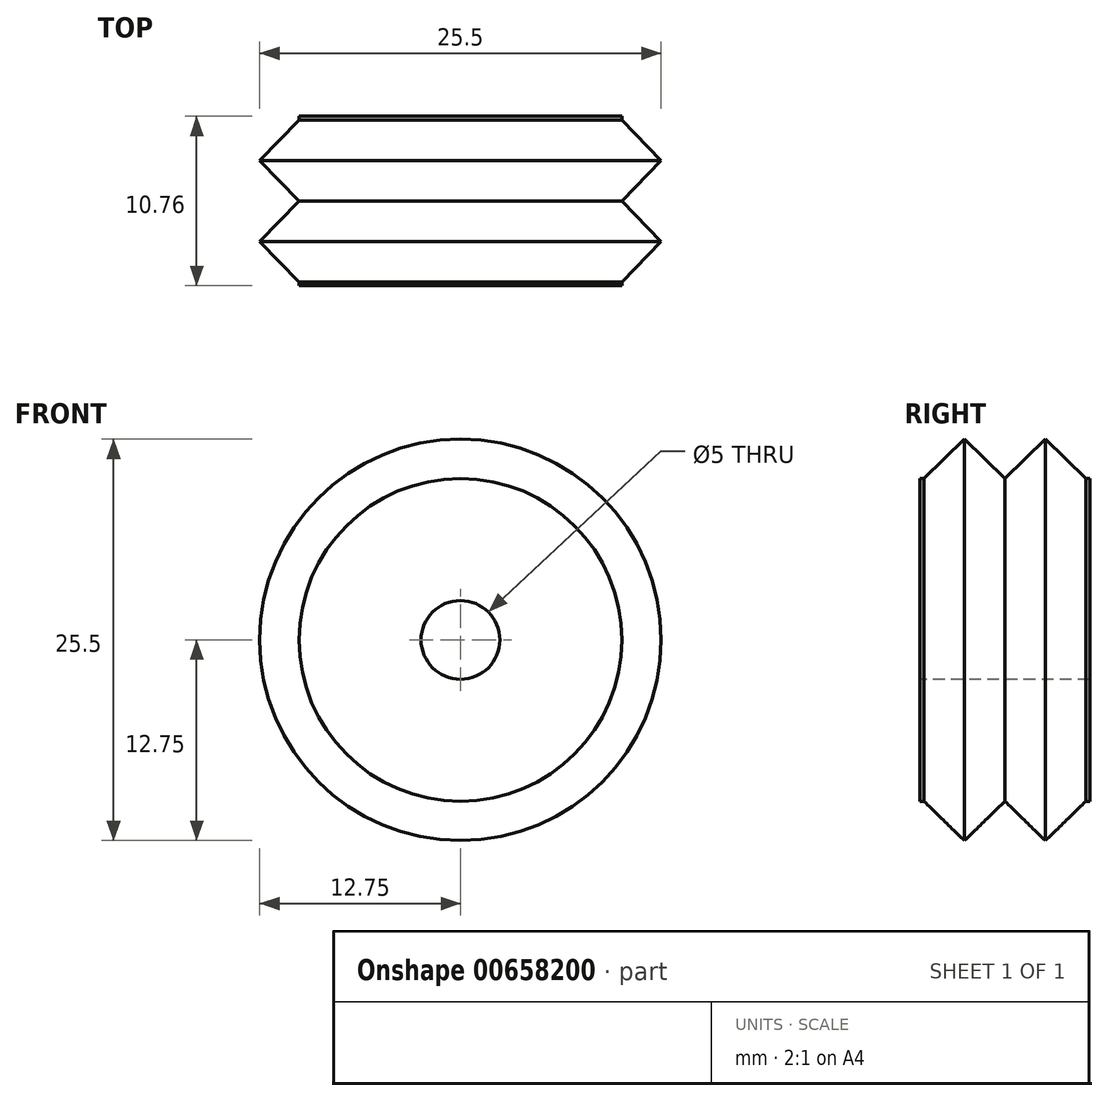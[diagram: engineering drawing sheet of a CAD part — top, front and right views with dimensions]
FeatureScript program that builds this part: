
annotation { "Feature Type Name" : "Feature", "Feature Type Description" : "" }
export const myFeature = defineFeature(function(context is Context, id is Id, definition is map)
    precondition{}
    {
        {
            var Q0;
            Q0=qCreatedBy(makeId("Right.planeOp"),FACE);
            var sketch = newSketch(context, id + "F0", { "sketchPlane" : qUnion([Q0])});
            skPoint(sketch, "E0", {"position": v(0, 10.25) * mm});
            skLineSegment(sketch, "E1", {"start": v(0, 10.25) * mm, "end": v(2.57, 12.75) * mm});
            skLineSegment(sketch, "E2", {"start": v(2.57, 12.75) * mm, "end": v(5.14, 10.25) * mm});
            skLineSegment(sketch, "E3.MirrorCS", {"start": v(0, 10.25) * mm, "end": v(-2.57, 12.75) * mm});
            skLineSegment(sketch, "E4.MirrorCS", {"start": v(-2.57, 12.75) * mm, "end": v(-5.14, 10.25) * mm});
            skLineSegment(sketch, "E5", {"start": v(-5.14, 10.25) * mm, "end": v(-5.38, 10.25) * mm});
            skLineSegment(sketch, "E6", {"start": v(5.14, 10.25) * mm, "end": v(5.38, 10.25) * mm});
            skLineSegment(sketch, "E7", {"start": v(-5.38, 10.25) * mm, "end": v(-5.38, 2.5) * mm});
            skLineSegment(sketch, "E8", {"start": v(-5.38, 2.5) * mm, "end": v(5.38, 2.5) * mm});
            skLineSegment(sketch, "E9", {"start": v(5.38, 2.5) * mm, "end": v(5.38, 10.25) * mm});
            skLineSegment(sketch, "E10", {"start": v(-29.56, 0) * mm, "end": v(32.28, 0) * mm, "construction": true});
            skSolve(sketch);
        }
        {
            var Q0;
            Q0=makeQuery(id+"F0.imprint","IMPRINT",FACE,{"disambiguationData":[TD([[makeQuery(id+"F0.imprint","IMPRINT",EDGE,{"derivedFrom":sQuery(id+"F0.wireOp",EDGE,"E1")}),-1.0]])]});
            var Q1;
            Q1=sQuery(id+"F0.wireOp",EDGE,"E10");
            revolve(context, id + "F1", {"entities" : qUnion([Q0]), "axis" : qUnion([Q1]), "revolveType" : RevolveType.FULL});
        }
    });
